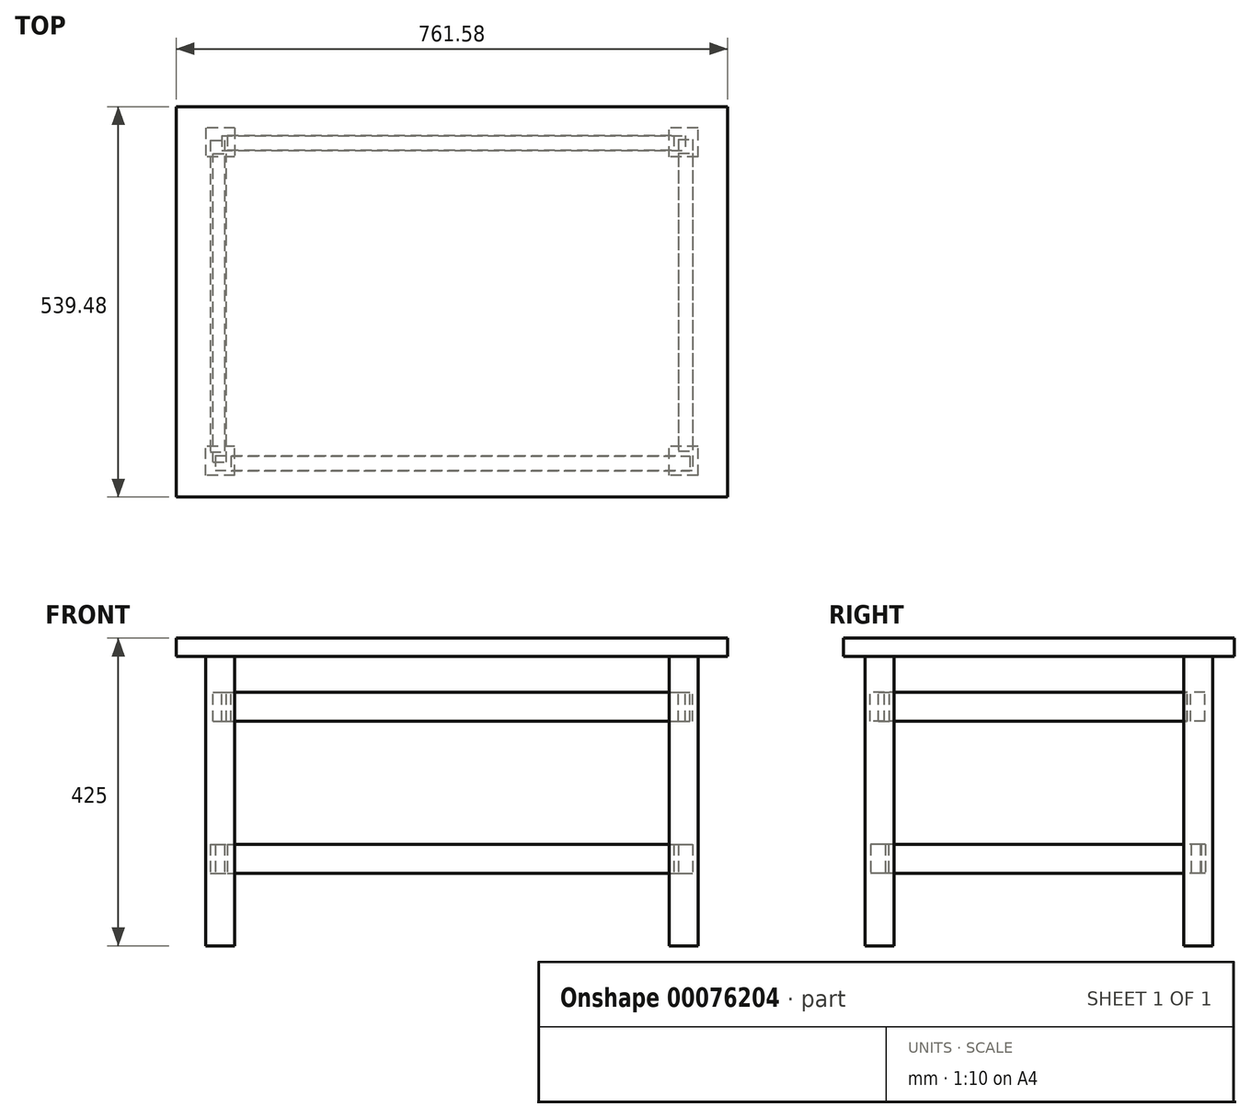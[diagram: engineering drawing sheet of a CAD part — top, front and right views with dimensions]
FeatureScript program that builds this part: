
annotation { "Feature Type Name" : "Feature", "Feature Type Description" : "" }
export const myFeature = defineFeature(function(context is Context, id is Id, definition is map)
    precondition{}
    {
        {
            var Q0;
            Q0=qCreatedBy(makeId("Top.planeOp"),FACE);
            var sketch = newSketch(context, id + "F0", { "sketchPlane" : qUnion([Q0])});
            skLineSegment(sketch, "E0.bottom", {"start": v(320, 220) * mm, "end": v(-320, 220) * mm});
            skLineSegment(sketch, "E0.top", {"start": v(320, -220) * mm, "end": v(-320, -220) * mm});
            skLineSegment(sketch, "E0.left", {"start": v(320, 220) * mm, "end": v(320, -220) * mm});
            skLineSegment(sketch, "E0.right", {"start": v(-320, 220) * mm, "end": v(-320, -220) * mm});
            skPoint(sketch, "E0.middle", {"position": v(0, 0) * mm});
            skLineSegment(sketch, "E1.bottom", {"start": v(-300, 240) * mm, "end": v(-340, 240) * mm});
            skLineSegment(sketch, "E1.top", {"start": v(-300, 200) * mm, "end": v(-340, 200) * mm});
            skLineSegment(sketch, "E1.left", {"start": v(-300, 240) * mm, "end": v(-300, 200) * mm});
            skLineSegment(sketch, "E1.right", {"start": v(-340, 240) * mm, "end": v(-340, 200) * mm});
            skPoint(sketch, "E1.middle", {"position": v(-320, 220) * mm});
            skLineSegment(sketch, "E2.bottom", {"start": v(-300, -240) * mm, "end": v(-340, -240) * mm});
            skLineSegment(sketch, "E2.top", {"start": v(-300, -200) * mm, "end": v(-340, -200) * mm});
            skLineSegment(sketch, "E2.left", {"start": v(-300, -240) * mm, "end": v(-300, -200) * mm});
            skLineSegment(sketch, "E2.right", {"start": v(-340, -240) * mm, "end": v(-340, -200) * mm});
            skPoint(sketch, "E2.middle", {"position": v(-320, -220) * mm});
            skLineSegment(sketch, "E3.bottom", {"start": v(340, -240) * mm, "end": v(300, -240) * mm});
            skLineSegment(sketch, "E3.top", {"start": v(340, -200) * mm, "end": v(300, -200) * mm});
            skLineSegment(sketch, "E3.left", {"start": v(340, -240) * mm, "end": v(340, -200) * mm});
            skLineSegment(sketch, "E3.right", {"start": v(300, -240) * mm, "end": v(300, -200) * mm});
            skPoint(sketch, "E3.middle", {"position": v(320, -220) * mm});
            skLineSegment(sketch, "E4.bottom", {"start": v(340, 200) * mm, "end": v(300, 200) * mm});
            skLineSegment(sketch, "E4.top", {"start": v(340, 240) * mm, "end": v(300, 240) * mm});
            skLineSegment(sketch, "E4.left", {"start": v(340, 200) * mm, "end": v(340, 240) * mm});
            skLineSegment(sketch, "E4.right", {"start": v(300, 200) * mm, "end": v(300, 240) * mm});
            skPoint(sketch, "E4.middle", {"position": v(320, 220) * mm});
            skSolve(sketch);
        }
        {
            var Q0;
            {var subQ4=sQuery(id+"F0.wireOp",EDGE,"E1.bottom");Q0=makeQuery(id+"F0.imprint","IMPRINT",FACE,{"disambiguationData":[TD([[makeQuery(id+"F0.imprint","IMPRINT",EDGE,{"derivedFrom":subQ4}),1.0]])]});}
            var Q1;
            {var subQ0=sQuery(id+"F0.wireOp",EDGE,"E0.right");var subQ1=sQuery(id+"F0.wireOp",EDGE,"E0.bottom");var subQ2=makeQuery(id+"F0.imprint","INTERSECT",VERTEX,{"derivedFrom":[subQ1,subQ0]});Q1=makeQuery(id+"F0.imprint","IMPRINT",FACE,{"disambiguationData":[TD([[makeQuery(id+"F0.imprint","IMPRINT",EDGE,{"disambiguationData":[TD([[subQ2,1.0]])],"derivedFrom":subQ1}),1.0]])]});}
            var Q2;
            {var subQ0=sQuery(id+"F0.wireOp",EDGE,"E0.left");var subQ1=sQuery(id+"F0.wireOp",EDGE,"E0.bottom");var subQ2=makeQuery(id+"F0.imprint","INTERSECT",VERTEX,{"derivedFrom":[subQ1,subQ0]});Q2=makeQuery(id+"F0.imprint","IMPRINT",FACE,{"disambiguationData":[TD([[makeQuery(id+"F0.imprint","IMPRINT",EDGE,{"disambiguationData":[TD([[subQ2,-1.0]])],"derivedFrom":subQ1}),1.0]])]});}
            var Q3;
            {var subQ6=sQuery(id+"F0.wireOp",EDGE,"E4.top");Q3=makeQuery(id+"F0.imprint","IMPRINT",FACE,{"disambiguationData":[TD([[makeQuery(id+"F0.imprint","IMPRINT",EDGE,{"derivedFrom":subQ6}),1.0]])]});}
            var Q4;
            {var subQ0=sQuery(id+"F0.wireOp",EDGE,"E0.left");var subQ1=sQuery(id+"F0.wireOp",EDGE,"E0.top");var subQ2=makeQuery(id+"F0.imprint","INTERSECT",VERTEX,{"derivedFrom":[subQ1,subQ0]});Q4=makeQuery(id+"F0.imprint","IMPRINT",FACE,{"disambiguationData":[TD([[makeQuery(id+"F0.imprint","IMPRINT",EDGE,{"disambiguationData":[TD([[subQ2,-1.0]])],"derivedFrom":subQ1}),-1.0]])]});}
            var Q5;
            {var subQ4=sQuery(id+"F0.wireOp",EDGE,"E3.bottom");Q5=makeQuery(id+"F0.imprint","IMPRINT",FACE,{"disambiguationData":[TD([[makeQuery(id+"F0.imprint","IMPRINT",EDGE,{"derivedFrom":subQ4}),-1.0]])]});}
            var Q6;
            {var subQ0=sQuery(id+"F0.wireOp",EDGE,"E0.right");var subQ1=sQuery(id+"F0.wireOp",EDGE,"E0.top");var subQ2=makeQuery(id+"F0.imprint","INTERSECT",VERTEX,{"derivedFrom":[subQ1,subQ0]});Q6=makeQuery(id+"F0.imprint","IMPRINT",FACE,{"disambiguationData":[TD([[makeQuery(id+"F0.imprint","IMPRINT",EDGE,{"disambiguationData":[TD([[subQ2,1.0]])],"derivedFrom":subQ1}),-1.0]])]});}
            var Q7;
            {var subQ0=sQuery(id+"F0.wireOp",EDGE,"E2.bottom");Q7=makeQuery(id+"F0.imprint","IMPRINT",FACE,{"disambiguationData":[TD([[makeQuery(id+"F0.imprint","IMPRINT",EDGE,{"derivedFrom":subQ0}),-1.0]])]});}
            extrude(context, id + "F1", {"entities" : qUnion([Q0, Q1, Q2, Q3, Q4, Q5, Q6, Q7]), "oppositeDirection" : true, "depth" : 400 * mm});
        }
        {
            var Q0;
            Q0=qCreatedBy(makeId("Top.planeOp"),FACE);
            cPlane(context, id + "F2", {"entities" : qUnion([Q0]), "cplaneType" : CPlaneType.OFFSET, "offset" : 50 * mm, "oppositeDirection" : true, "width" : 150 * mm, "height" : 150 * mm});
        }
        {
            var Q0;
            Q0=qCreatedBy(id+"F2.planeOp",FACE);
            var sketch = newSketch(context, id + "F3", { "sketchPlane" : qUnion([Q0])});
            skLineSegment(sketch, "E5.bottom", {"start": v(-318.1, 229.3) * mm, "end": v(321.9, 229.3) * mm});
            skLineSegment(sketch, "E5.top", {"start": v(-318.1, 209.3) * mm, "end": v(321.9, 209.3) * mm});
            skLineSegment(sketch, "E5.left", {"start": v(-318.1, 229.3) * mm, "end": v(-318.1, 209.3) * mm});
            skLineSegment(sketch, "E5.right", {"start": v(321.9, 229.3) * mm, "end": v(321.9, 209.3) * mm});
            skLineSegment(sketch, "E6.bottom", {"start": v(-329.9, -221.46) * mm, "end": v(-311.46, -221.46) * mm});
            skLineSegment(sketch, "E6.top", {"start": v(-329.9, 204.66) * mm, "end": v(-311.46, 204.66) * mm});
            skLineSegment(sketch, "E6.left", {"start": v(-329.9, -221.46) * mm, "end": v(-329.9, 204.66) * mm});
            skLineSegment(sketch, "E6.right", {"start": v(-311.46, -221.46) * mm, "end": v(-311.46, 204.66) * mm});
            skLineSegment(sketch, "E7.bottom", {"start": v(-305.5, -213.4) * mm, "end": v(328.27, -213.4) * mm});
            skLineSegment(sketch, "E7.top", {"start": v(-305.5, -233.4) * mm, "end": v(328.27, -233.4) * mm});
            skLineSegment(sketch, "E7.left", {"start": v(-305.5, -213.4) * mm, "end": v(-305.5, -233.4) * mm});
            skLineSegment(sketch, "E7.right", {"start": v(328.27, -213.4) * mm, "end": v(328.27, -233.4) * mm});
            skLineSegment(sketch, "E8.bottom", {"start": v(312.6, 205.2) * mm, "end": v(332.6, 205.2) * mm});
            skLineSegment(sketch, "E8.top", {"start": v(312.6, -206.28) * mm, "end": v(332.6, -206.28) * mm});
            skLineSegment(sketch, "E8.left", {"start": v(312.6, 205.2) * mm, "end": v(312.6, -206.28) * mm});
            skLineSegment(sketch, "E8.right", {"start": v(332.6, 205.2) * mm, "end": v(332.6, -206.28) * mm});
            skSolve(sketch);
        }
        {
            var Q0;
            Q0=makeQuery(id+"F3.imprint","IMPRINT",FACE,{"disambiguationData":[TD([[makeQuery(id+"F3.imprint","IMPRINT",EDGE,{"derivedFrom":sQuery(id+"F3.wireOp",EDGE,"E6.bottom")}),1.0]])]});
            var Q1;
            Q1=makeQuery(id+"F3.imprint","IMPRINT",FACE,{"disambiguationData":[TD([[makeQuery(id+"F3.imprint","IMPRINT",EDGE,{"derivedFrom":sQuery(id+"F3.wireOp",EDGE,"E5.bottom")}),-1.0]])]});
            var Q2;
            Q2=makeQuery(id+"F3.imprint","IMPRINT",FACE,{"disambiguationData":[TD([[makeQuery(id+"F3.imprint","IMPRINT",EDGE,{"derivedFrom":sQuery(id+"F3.wireOp",EDGE,"E8.bottom")}),-1.0]])]});
            var Q3;
            Q3=makeQuery(id+"F3.imprint","IMPRINT",FACE,{"disambiguationData":[TD([[makeQuery(id+"F3.imprint","IMPRINT",EDGE,{"derivedFrom":sQuery(id+"F3.wireOp",EDGE,"E7.bottom")}),-1.0]])]});
            extrude(context, id + "F4", {"entities" : qUnion([Q0, Q1, Q2, Q3]), "oppositeDirection" : true, "depth" : 40 * mm});
        }
        {
            var Q0;
            Q0=qCreatedBy(makeId("Top.planeOp"),FACE);
            cPlane(context, id + "F5", {"entities" : qUnion([Q0]), "cplaneType" : CPlaneType.OFFSET, "offset" : 300 * mm, "oppositeDirection" : true, "width" : 150 * mm, "height" : 150 * mm});
        }
        {
            var Q0;
            Q0=qCreatedBy(id+"F5.planeOp",FACE);
            var sketch = newSketch(context, id + "F6", { "sketchPlane" : qUnion([Q0])});
            skLineSegment(sketch, "E9.bottom", {"start": v(312.32, 224.36) * mm, "end": v(332.32, 224.36) * mm});
            skLineSegment(sketch, "E9.top", {"start": v(312.32, -224.36) * mm, "end": v(332.32, -224.36) * mm});
            skLineSegment(sketch, "E9.left", {"start": v(312.32, 224.36) * mm, "end": v(312.32, -224.36) * mm});
            skLineSegment(sketch, "E9.right", {"start": v(332.32, 224.36) * mm, "end": v(332.32, -224.36) * mm});
            skLineSegment(sketch, "E10.bottom", {"start": v(-327.07, -212.48) * mm, "end": v(332.32, -212.48) * mm});
            skLineSegment(sketch, "E10.top", {"start": v(-327.07, -232.48) * mm, "end": v(332.32, -232.48) * mm});
            skLineSegment(sketch, "E10.left", {"start": v(-327.07, -212.48) * mm, "end": v(-327.07, -232.48) * mm});
            skLineSegment(sketch, "E10.right", {"start": v(332.32, -212.48) * mm, "end": v(332.32, -232.48) * mm});
            skLineSegment(sketch, "E11.bottom", {"start": v(-334.08, 222.97) * mm, "end": v(-314.08, 222.97) * mm});
            skLineSegment(sketch, "E11.top", {"start": v(-334.08, -207.46) * mm, "end": v(-314.08, -207.46) * mm});
            skLineSegment(sketch, "E11.left", {"start": v(-334.08, 222.97) * mm, "end": v(-334.08, -207.46) * mm});
            skLineSegment(sketch, "E11.right", {"start": v(-314.08, 222.97) * mm, "end": v(-314.08, -207.46) * mm});
            skLineSegment(sketch, "E12.bottom", {"start": v(-310.06, 229.96) * mm, "end": v(306.55, 229.96) * mm});
            skLineSegment(sketch, "E12.top", {"start": v(-310.06, 209.96) * mm, "end": v(306.55, 209.96) * mm});
            skLineSegment(sketch, "E12.left", {"start": v(-310.06, 229.96) * mm, "end": v(-310.06, 209.96) * mm});
            skLineSegment(sketch, "E12.right", {"start": v(306.55, 229.96) * mm, "end": v(306.55, 209.96) * mm});
            skSolve(sketch);
        }
        {
            var Q0;
            Q0 = qSketchRegion(id + "F6", true);
            extrude(context, id + "F7", {"entities" : qUnion([Q0]), "depth" : 40 * mm});
        }
        {
            var Q0;
            Q0=qCreatedBy(makeId("Top.planeOp"),FACE);
            var sketch = newSketch(context, id + "F8", { "sketchPlane" : qUnion([Q0])});
            skLineSegment(sketch, "E13.bottom", {"start": v(380.79, -269.74) * mm, "end": v(-380.79, -269.74) * mm});
            skLineSegment(sketch, "E13.top", {"start": v(380.79, 269.74) * mm, "end": v(-380.79, 269.74) * mm});
            skLineSegment(sketch, "E13.left", {"start": v(380.79, -269.74) * mm, "end": v(380.79, 269.74) * mm});
            skLineSegment(sketch, "E13.right", {"start": v(-380.79, -269.74) * mm, "end": v(-380.79, 269.74) * mm});
            skPoint(sketch, "E13.middle", {"position": v(0, 0) * mm});
            skSolve(sketch);
        }
        {
            var Q0;
            Q0=makeQuery(id+"F8.imprint","IMPRINT",FACE,{"disambiguationData":[TD([[makeQuery(id+"F8.imprint","IMPRINT",EDGE,{"derivedFrom":sQuery(id+"F8.wireOp",EDGE,"E13.bottom")}),-1.0]])]});
            extrude(context, id + "F9", {"entities" : qUnion([Q0]), "depth" : 25 * mm});
        }
    });
